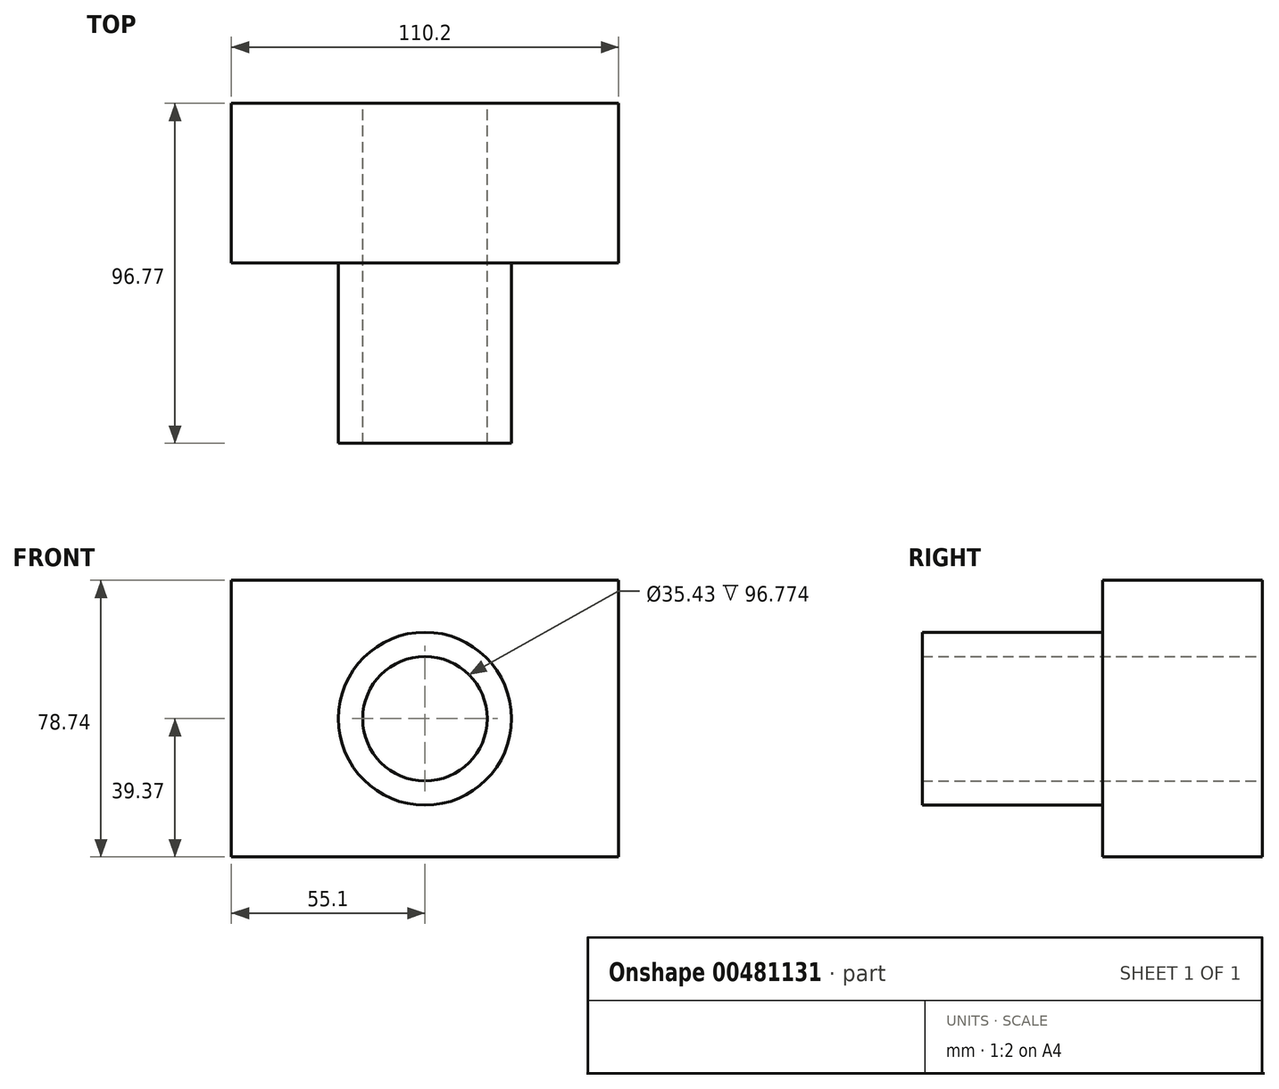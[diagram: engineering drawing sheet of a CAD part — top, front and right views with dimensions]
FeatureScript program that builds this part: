
annotation { "Feature Type Name" : "Feature", "Feature Type Description" : "" }
export const myFeature = defineFeature(function(context is Context, id is Id, definition is map)
    precondition{}
    {
        {
            var Q0;
            Q0=qCreatedBy(makeId("Front.planeOp"),FACE);
            var sketch = newSketch(context, id + "F0", { "sketchPlane" : qUnion([Q0])});
            skLineSegment(sketch, "E0.bottom", {"start": v(55.1, -39.37) * mm, "end": v(-55.1, -39.37) * mm});
            skLineSegment(sketch, "E0.top", {"start": v(55.1, 39.37) * mm, "end": v(-55.1, 39.37) * mm});
            skLineSegment(sketch, "E0.left", {"start": v(55.1, -39.37) * mm, "end": v(55.1, 39.37) * mm});
            skLineSegment(sketch, "E0.right", {"start": v(-55.1, -39.37) * mm, "end": v(-55.1, 39.37) * mm});
            skPoint(sketch, "E0.middle", {"position": v(0, 0) * mm});
            skCircle(sketch, "E1", {"center": v(0, 0) * mm, "radius": 24.62 * mm});
            skCircle(sketch, "E2", {"center": v(0, 0) * mm, "radius": 17.72 * mm});
            skSolve(sketch);
        }
        {
            var Q0;
            Q0=makeQuery(id+"F0.imprint","IMPRINT",FACE,{"disambiguationData":[TD([[makeQuery(id+"F0.imprint","IMPRINT",EDGE,{"derivedFrom":sQuery(id+"F0.wireOp",EDGE,"E1")}),1.0]])]});
            extrude(context, id + "F1", {"entities" : qUnion([Q0]), "depth" : 96.77 * mm});
        }
        {
            var Q0;
            Q0 = qSketchRegion(id + "F0", true);
            extrude(context, id + "F2", {"entities" : qUnion([Q0]), "operationType" : NewBodyOperationType.ADD, "depth" : 45.47 * mm});
        }
    });
